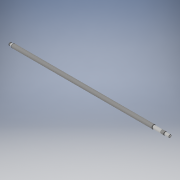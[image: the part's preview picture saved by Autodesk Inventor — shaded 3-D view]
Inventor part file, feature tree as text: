
AUTODESK INVENTOR PART (.ipt)
format: ipt  version: 2021 (Build 250183000, 183)  size: 156,672 bytes
history: native  units: mm
features: other x21, revolve x2, thread x2, sketch x1
ambient origin geometry x8: Origin, YZ Plane, XZ Plane, XY Plane, X Axis, Y Axis, Z Axis, Center Point
bodies: Solid1 (feature_tree)
feature tree (26):
  revolve  "Revolution1"  [1 undecoded]
  thread  "Thread1"  [1 undecoded]
  revolve  "Revolution2"  [1 undecoded]
  thread  "Thread2"  [1 undecoded]
  other  "to_collar_XY"
  other  "to_collar_YZ"
  other  "to_collar_ZX"
  other  "to_collar_X"
  other  "to_collar_Y"
  other  "to_collar_Z"
  other  "to_collar_Center"
  other  "to_dummy_XY"
  other  "to_dummy_YZ"
  other  "to_dummy_ZX"
  other  "to_dummy_X"
  other  "to_dummy_Y"
  other  "to_dummy_Z"
  other  "to_dummy_Center"
  other  "to_nut_XY"
  other  "to_nut_YZ"
  other  "to_nut_ZX"
  other  "to_nut_X"
  other  "to_nut_Y"
  other  "to_nut_Z"
  other  "to_nut_Center"
  sketch  "Sketch_1"  dims[d0=360.0deg d1=438.0mm d2=0.0mm d3=360.0deg d4=10.5mm d5=0.0mm d6=0.0mm]
note: 4 required parameter values undecoded (feature->parameter linkage not recoverable at this tier; creation-order binding heuristic only, values carry confidence <= 0.55)